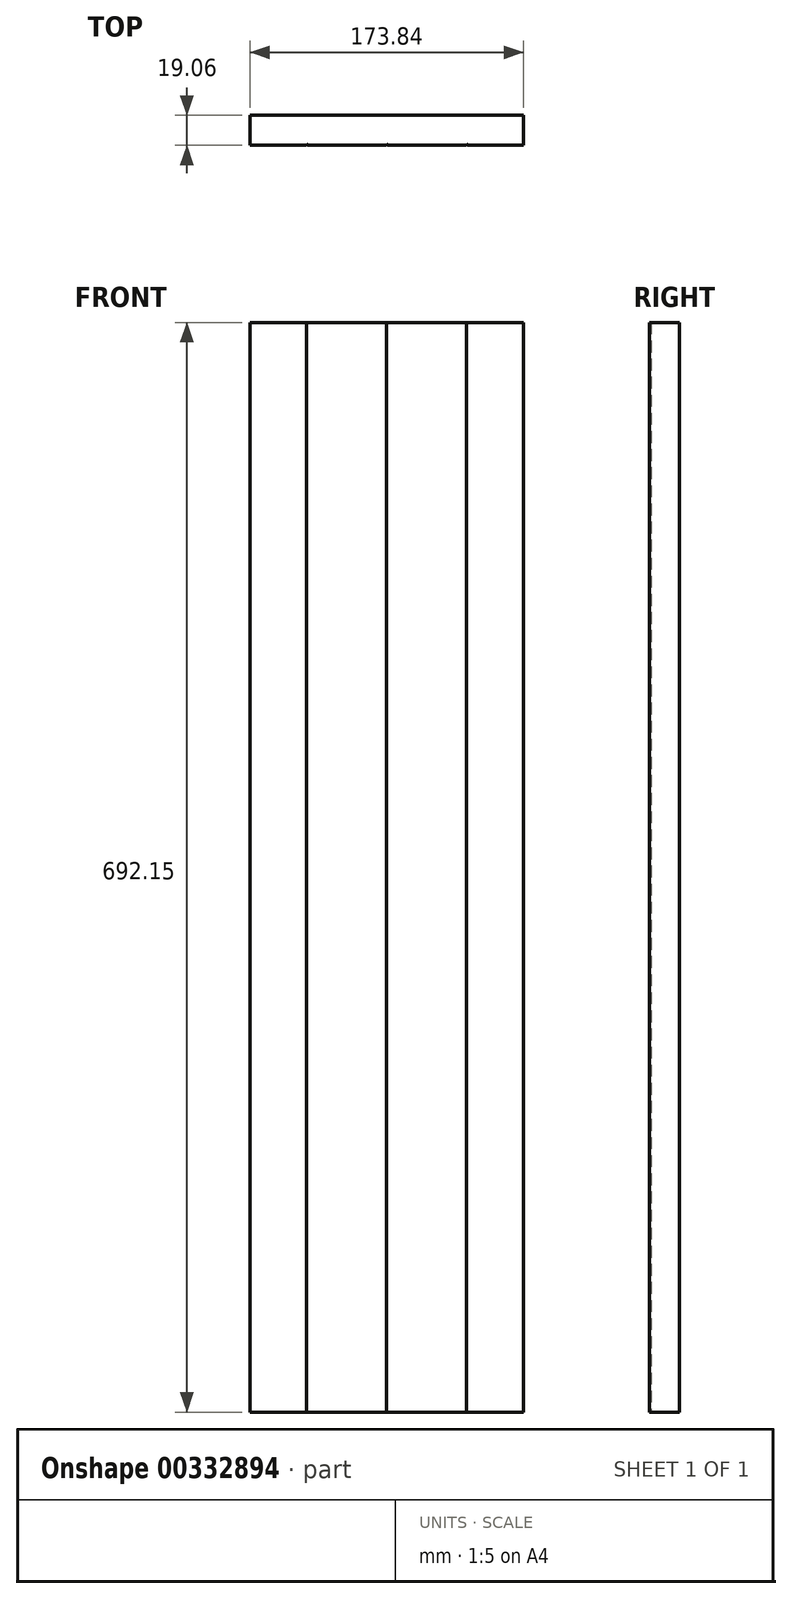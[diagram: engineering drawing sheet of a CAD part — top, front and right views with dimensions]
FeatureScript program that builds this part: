
annotation { "Feature Type Name" : "Feature", "Feature Type Description" : "" }
export const myFeature = defineFeature(function(context is Context, id is Id, definition is map)
    precondition{}
    {
        {
            var Q0;
            Q0=qCreatedBy(makeId("Top.planeOp"),FACE);
            var sketch = newSketch(context, id + "F0", { "sketchPlane" : qUnion([Q0])});
            skLineSegment(sketch, "E0.bottom", {"start": v(508, -9.53) * mm, "end": v(458.22, -9.53) * mm});
            skLineSegment(sketch, "E0.top", {"start": v(508, 9.53) * mm, "end": v(-508, 9.53) * mm});
            skLineSegment(sketch, "E0.left", {"start": v(508, 9.53) * mm, "end": v(508, -9.53) * mm});
            skLineSegment(sketch, "E0.right", {"start": v(-508, 9.53) * mm, "end": v(-508, -9.53) * mm});
            skPoint(sketch, "E0.middle", {"position": v(0, 0) * mm});
            skArc(sketch, "E1", {"start": v(-509.02, -9.53) * mm, "mid": v(-508.3, -9.23) * mm, "end": v(-508, -8.5) * mm});
            skArc(sketch, "E2", {"start": v(-508, -8.5) * mm, "mid": v(-507.7, -9.23) * mm, "end": v(-506.98, -9.52) * mm});
            skArc(sketch, "E3.1.0.0", {"start": v(-458.22, -9.53) * mm, "mid": v(-457.5, -9.23) * mm, "end": v(-457.2, -8.5) * mm});
            skArc(sketch, "E3.1.0.1", {"start": v(-457.2, -8.5) * mm, "mid": v(-456.9, -9.23) * mm, "end": v(-456.18, -9.52) * mm});
            skArc(sketch, "E3.2.0.0", {"start": v(-407.42, -9.53) * mm, "mid": v(-406.7, -9.23) * mm, "end": v(-406.4, -8.5) * mm});
            skArc(sketch, "E3.2.0.1", {"start": v(-406.4, -8.5) * mm, "mid": v(-406.1, -9.23) * mm, "end": v(-405.38, -9.52) * mm});
            skArc(sketch, "E3.3.0.0", {"start": v(-356.62, -9.53) * mm, "mid": v(-355.9, -9.23) * mm, "end": v(-355.6, -8.5) * mm});
            skArc(sketch, "E3.3.0.1", {"start": v(-355.6, -8.5) * mm, "mid": v(-355.3, -9.23) * mm, "end": v(-354.58, -9.52) * mm});
            skArc(sketch, "E3.4.0.0", {"start": v(-305.82, -9.53) * mm, "mid": v(-305.1, -9.23) * mm, "end": v(-304.8, -8.5) * mm});
            skArc(sketch, "E3.4.0.1", {"start": v(-304.8, -8.5) * mm, "mid": v(-304.5, -9.23) * mm, "end": v(-303.78, -9.52) * mm});
            skArc(sketch, "E3.5.0.0", {"start": v(-255.02, -9.53) * mm, "mid": v(-254.3, -9.23) * mm, "end": v(-254, -8.5) * mm});
            skArc(sketch, "E3.5.0.1", {"start": v(-254, -8.5) * mm, "mid": v(-253.7, -9.23) * mm, "end": v(-252.98, -9.52) * mm});
            skArc(sketch, "E3.6.0.0", {"start": v(-204.22, -9.53) * mm, "mid": v(-203.5, -9.23) * mm, "end": v(-203.2, -8.5) * mm});
            skArc(sketch, "E3.6.0.1", {"start": v(-203.2, -8.5) * mm, "mid": v(-202.9, -9.23) * mm, "end": v(-202.18, -9.52) * mm});
            skArc(sketch, "E3.7.0.0", {"start": v(-153.42, -9.53) * mm, "mid": v(-152.7, -9.23) * mm, "end": v(-152.4, -8.5) * mm});
            skArc(sketch, "E3.7.0.1", {"start": v(-152.4, -8.5) * mm, "mid": v(-152.1, -9.23) * mm, "end": v(-151.38, -9.52) * mm});
            skArc(sketch, "E3.8.0.0", {"start": v(-102.62, -9.53) * mm, "mid": v(-101.9, -9.23) * mm, "end": v(-101.6, -8.5) * mm});
            skArc(sketch, "E3.8.0.1", {"start": v(-101.6, -8.5) * mm, "mid": v(-101.3, -9.23) * mm, "end": v(-100.58, -9.52) * mm});
            skArc(sketch, "E3.9.0.0", {"start": v(-51.82, -9.53) * mm, "mid": v(-51.1, -9.23) * mm, "end": v(-50.8, -8.5) * mm});
            skArc(sketch, "E3.9.0.1", {"start": v(-50.8, -8.5) * mm, "mid": v(-50.5, -9.23) * mm, "end": v(-49.78, -9.52) * mm});
            skArc(sketch, "E3.10.0.0", {"start": v(-1.02, -9.53) * mm, "mid": v(-0.3, -9.23) * mm, "end": v(0, -8.5) * mm});
            skArc(sketch, "E3.10.0.1", {"start": v(0, -8.5) * mm, "mid": v(0.3, -9.23) * mm, "end": v(1.02, -9.52) * mm});
            skArc(sketch, "E3.11.0.0", {"start": v(49.78, -9.53) * mm, "mid": v(50.5, -9.23) * mm, "end": v(50.8, -8.5) * mm});
            skArc(sketch, "E3.11.0.1", {"start": v(50.8, -8.5) * mm, "mid": v(51.1, -9.23) * mm, "end": v(51.82, -9.52) * mm});
            skArc(sketch, "E3.12.0.0", {"start": v(100.58, -9.53) * mm, "mid": v(101.3, -9.23) * mm, "end": v(101.6, -8.5) * mm});
            skArc(sketch, "E3.12.0.1", {"start": v(101.6, -8.5) * mm, "mid": v(101.9, -9.23) * mm, "end": v(102.62, -9.52) * mm});
            skArc(sketch, "E3.13.0.0", {"start": v(151.38, -9.53) * mm, "mid": v(152.1, -9.23) * mm, "end": v(152.4, -8.5) * mm});
            skArc(sketch, "E3.13.0.1", {"start": v(152.4, -8.5) * mm, "mid": v(152.7, -9.23) * mm, "end": v(153.42, -9.52) * mm});
            skArc(sketch, "E3.14.0.0", {"start": v(202.18, -9.53) * mm, "mid": v(202.9, -9.23) * mm, "end": v(203.2, -8.5) * mm});
            skArc(sketch, "E3.14.0.1", {"start": v(203.2, -8.5) * mm, "mid": v(203.5, -9.23) * mm, "end": v(204.22, -9.52) * mm});
            skArc(sketch, "E3.15.0.0", {"start": v(252.98, -9.53) * mm, "mid": v(253.7, -9.23) * mm, "end": v(254, -8.5) * mm});
            skArc(sketch, "E3.15.0.1", {"start": v(254, -8.5) * mm, "mid": v(254.3, -9.23) * mm, "end": v(255.02, -9.52) * mm});
            skArc(sketch, "E3.16.0.0", {"start": v(303.78, -9.53) * mm, "mid": v(304.5, -9.23) * mm, "end": v(304.8, -8.5) * mm});
            skArc(sketch, "E3.16.0.1", {"start": v(304.8, -8.5) * mm, "mid": v(305.1, -9.23) * mm, "end": v(305.82, -9.52) * mm});
            skArc(sketch, "E3.17.0.0", {"start": v(354.58, -9.53) * mm, "mid": v(355.3, -9.23) * mm, "end": v(355.6, -8.5) * mm});
            skArc(sketch, "E3.17.0.1", {"start": v(355.6, -8.5) * mm, "mid": v(355.9, -9.23) * mm, "end": v(356.62, -9.52) * mm});
            skArc(sketch, "E3.18.0.0", {"start": v(405.38, -9.53) * mm, "mid": v(406.1, -9.23) * mm, "end": v(406.4, -8.5) * mm});
            skArc(sketch, "E3.18.0.1", {"start": v(406.4, -8.5) * mm, "mid": v(406.7, -9.23) * mm, "end": v(407.42, -9.52) * mm});
            skArc(sketch, "E3.19.0.0", {"start": v(456.18, -9.53) * mm, "mid": v(456.9, -9.23) * mm, "end": v(457.2, -8.5) * mm});
            skArc(sketch, "E3.19.0.1", {"start": v(457.2, -8.5) * mm, "mid": v(457.5, -9.23) * mm, "end": v(458.22, -9.52) * mm});
            skLineSegment(sketch, "E3.direction1", {"start": v(-506.98, -9.53) * mm, "end": v(-458.22, -9.53) * mm, "construction": true});
            skLineSegment(sketch, "E4.trimOffspring", {"start": v(-458.22, -9.53) * mm, "end": v(-508, -9.53) * mm});
            skLineSegment(sketch, "E5.trimOffspring", {"start": v(-407.42, -9.53) * mm, "end": v(-456.18, -9.53) * mm});
            skLineSegment(sketch, "E6.trimOffspring", {"start": v(-356.62, -9.53) * mm, "end": v(-405.38, -9.53) * mm});
            skLineSegment(sketch, "E7.trimOffspring", {"start": v(-305.82, -9.53) * mm, "end": v(-354.58, -9.53) * mm});
            skLineSegment(sketch, "E8.trimOffspring", {"start": v(-255.02, -9.53) * mm, "end": v(-303.78, -9.53) * mm});
            skLineSegment(sketch, "E9.trimOffspring", {"start": v(-204.22, -9.53) * mm, "end": v(-252.98, -9.53) * mm});
            skLineSegment(sketch, "E10.trimOffspring", {"start": v(-153.42, -9.53) * mm, "end": v(-202.18, -9.53) * mm});
            skLineSegment(sketch, "E11.trimOffspring", {"start": v(-102.62, -9.53) * mm, "end": v(-151.38, -9.53) * mm});
            skLineSegment(sketch, "E12.trimOffspring", {"start": v(-51.82, -9.53) * mm, "end": v(-100.58, -9.53) * mm});
            skLineSegment(sketch, "E13.trimOffspring", {"start": v(-1.02, -9.53) * mm, "end": v(-49.78, -9.53) * mm});
            skLineSegment(sketch, "E14.trimOffspring", {"start": v(49.78, -9.53) * mm, "end": v(1.02, -9.53) * mm});
            skLineSegment(sketch, "E15.trimOffspring", {"start": v(100.58, -9.53) * mm, "end": v(51.82, -9.53) * mm});
            skLineSegment(sketch, "E16.trimOffspring", {"start": v(151.38, -9.53) * mm, "end": v(102.62, -9.53) * mm});
            skLineSegment(sketch, "E17.trimOffspring", {"start": v(202.18, -9.53) * mm, "end": v(153.42, -9.53) * mm});
            skLineSegment(sketch, "E18.trimOffspring", {"start": v(252.98, -9.53) * mm, "end": v(204.22, -9.53) * mm});
            skLineSegment(sketch, "E19.trimOffspring", {"start": v(303.78, -9.53) * mm, "end": v(255.02, -9.53) * mm});
            skLineSegment(sketch, "E20.trimOffspring", {"start": v(354.58, -9.53) * mm, "end": v(305.82, -9.53) * mm});
            skLineSegment(sketch, "E21.trimOffspring", {"start": v(405.38, -9.53) * mm, "end": v(356.62, -9.53) * mm});
            skLineSegment(sketch, "E22.trimOffspring", {"start": v(456.18, -9.53) * mm, "end": v(407.42, -9.53) * mm});
            skSolve(sketch);
        }
        {
            var Q0;
            Q0=qSketchRegion(id+"F0",true);
            extrude(context, id + "F1", {"entities" : qUnion([Q0]), "depth" : 692.15 * mm});
        }
        {
            var Q0;
            Q0=qCreatedBy(makeId("Top.planeOp"),FACE);
            var sketch = newSketch(context, id + "F2", { "sketchPlane" : qUnion([Q0])});
            skLineSegment(sketch, "E23.bottom", {"start": v(86.92, -89.59) * mm, "end": v(594.92, -89.59) * mm});
            skLineSegment(sketch, "E23.top", {"start": v(86.92, 47.64) * mm, "end": v(594.92, 47.64) * mm});
            skLineSegment(sketch, "E23.left", {"start": v(86.92, -89.59) * mm, "end": v(86.92, 47.64) * mm});
            skLineSegment(sketch, "E23.right", {"start": v(594.92, -89.59) * mm, "end": v(594.92, 47.64) * mm});
            skLineSegment(sketch, "E24.bottom", {"start": v(-86.92, -137.09) * mm, "end": v(-594.92, -137.09) * mm});
            skLineSegment(sketch, "E24.top", {"start": v(-86.92, 58.2) * mm, "end": v(-594.92, 58.2) * mm});
            skLineSegment(sketch, "E24.left", {"start": v(-86.92, -137.09) * mm, "end": v(-86.92, 58.2) * mm});
            skLineSegment(sketch, "E24.right", {"start": v(-594.92, -137.09) * mm, "end": v(-594.92, 58.2) * mm});
            skSolve(sketch);
        }
        {
            var Q0;
            Q0=qSketchRegion(id+"F2",true);
            extrude(context, id + "F3", {"entities" : qUnion([Q0]), "operationType" : NewBodyOperationType.REMOVE, "depth" : 1143 * mm});
        }
    });
